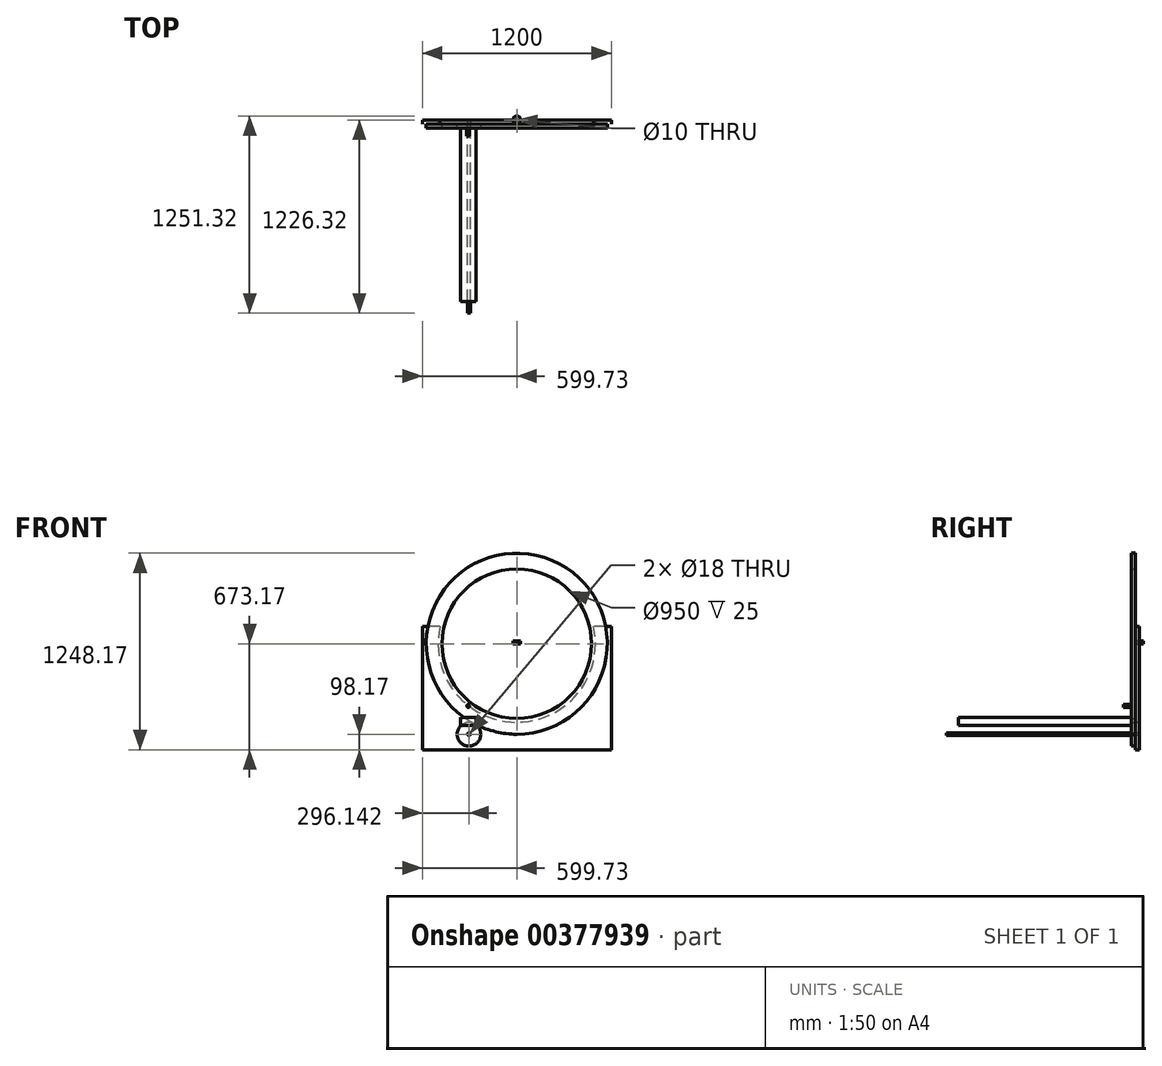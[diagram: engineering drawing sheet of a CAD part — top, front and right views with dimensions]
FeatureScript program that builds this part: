
annotation { "Feature Type Name" : "Feature", "Feature Type Description" : "" }
export const myFeature = defineFeature(function(context is Context, id is Id, definition is map)
    precondition{}
    {
        {
            var Q0;
            Q0=qCreatedBy(makeId("Front.planeOp"),FACE);
            var sketch = newSketch(context, id + "F0", { "sketchPlane" : qUnion([Q0])});
            skCircle(sketch, "E0", {"center": v(0, 0) * mm, "radius": 575 * mm});
            skCircle(sketch, "E1.0", {"center": v(0, 0) * mm, "radius": 475 * mm});
            skLineSegment(sketch, "E2", {"start": v(0, -575) * mm, "end": v(-1243.46, -575) * mm, "construction": true});
            skCircle(sketch, "E3", {"center": v(-303.59, -575) * mm, "radius": 75 * mm});
            skCircle(sketch, "E4", {"center": v(-303.59, -575) * mm, "radius": 9 * mm});
            skSolve(sketch);
        }
        {
            var Q0;
            Q0 = qSketchRegion(id + "F0", true);
            extrude(context, id + "F1", {"entities" : qUnion([Q0]), "depth" : 25 * mm});
        }
        {
            var Q0;
            Q0=makeQuery(id+"F0.imprint","IMPRINT",FACE,{"disambiguationData":[TD([[makeQuery(id+"F0.imprint","IMPRINT",EDGE,{"derivedFrom":sQuery(id+"F0.wireOp",EDGE,"E4")}),1.0]])]});
            extrude(context, id + "F2", {"entities" : qUnion([Q0]), "depth" : (48 * 25) * mm});
        }
        {
            var Q0;
            Q0=qCreatedBy(makeId("Top.planeOp"),FACE);
            var sketch = newSketch(context, id + "F3", { "sketchPlane" : qUnion([Q0])});
            skCircle(sketch, "E5", {"center": v(0, 26.32) * mm, "radius": 25 * mm});
            skCircle(sketch, "E6", {"center": v(0, 26.32) * mm, "radius": 5 * mm});
            skSolve(sketch);
        }
        {
            var Q0;
            Q0=makeQuery(id+"F3.imprint","IMPRINT",FACE,{"disambiguationData":[TD([[makeQuery(id+"F3.imprint","IMPRINT",EDGE,{"derivedFrom":sQuery(id+"F3.wireOp",EDGE,"E5")}),1.0]])]});
            extrude(context, id + "F4", {"entities" : qUnion([Q0]), "depth" : 18 * mm});
        }
        {
            var Q0;
            Q0=qCreatedBy(makeId("Front.planeOp"),FACE);
            var sketch = newSketch(context, id + "F5", { "sketchPlane" : qUnion([Q0])});
            skCircle(sketch, "E7", {"center": v(0, 0) * mm, "radius": 575 * mm});
            skCircle(sketch, "E8.0", {"center": v(0, 0) * mm, "radius": 475 * mm});
            skLineSegment(sketch, "E9", {"start": v(0, -575) * mm, "end": v(-1243.46, -575) * mm, "construction": true});
            skCircle(sketch, "E10", {"center": v(-303.59, -575) * mm, "radius": 75 * mm});
            skCircle(sketch, "E11", {"center": v(-303.59, -575) * mm, "radius": 9 * mm});
            skCircle(sketch, "E12", {"center": v(0, 0) * mm, "radius": 499.06 * mm});
            skPoint(sketch, "E13.firstSnap0", {"position": v(-621.73, -575) * mm});
            skLineSegment(sketch, "E13.bottom", {"start": v(-599.73, 526.83) * mm, "end": v(600.27, 526.83) * mm});
            skLineSegment(sketch, "E13.top", {"start": v(-599.73, -673.17) * mm, "end": v(600.27, -673.17) * mm});
            skLineSegment(sketch, "E13.left", {"start": v(-599.73, 526.83) * mm, "end": v(-599.73, -673.17) * mm});
            skLineSegment(sketch, "E13.right", {"start": v(600.27, 526.83) * mm, "end": v(600.27, -673.17) * mm});
            skLineSegment(sketch, "E14", {"start": v(707.26, 110.12) * mm, "end": v(-898.64, 110.12) * mm});
            skSolve(sketch);
        }
        {
            var Q0;
            Q0=makeQuery(id+"F5.imprint","IMPRINT",FACE,{"disambiguationData":[TD([[makeQuery(id+"F5.imprint","IMPRINT",EDGE,{"derivedFrom":sQuery(id+"F5.wireOp",EDGE,"E10")}),-1.0]])]});
            var Q1;
            {var subQ0=sQuery(id+"F5.wireOp",EDGE,"E14");var subQ1=sQuery(id+"F5.wireOp",EDGE,"E7");var subQ2=makeQuery(id+"F5.imprint","INTERSECT",VERTEX,{"disambiguationData":[OD(0.0)],"derivedFrom":[subQ1,subQ0]});Q1=makeQuery(id+"F5.imprint","IMPRINT",FACE,{"disambiguationData":[TD([[makeQuery(id+"F5.imprint","IMPRINT",EDGE,{"disambiguationData":[TD([[subQ2,1.0]])],"derivedFrom":subQ1}),1.0]])]});}
            var Q2;
            Q2=makeQuery(id+"F5.imprint","IMPRINT",FACE,{"disambiguationData":[TD([[makeQuery(id+"F5.imprint","IMPRINT",EDGE,{"derivedFrom":sQuery(id+"F5.wireOp",EDGE,"E10")}),1.0]])]});
            extrude(context, id + "F6", {"entities" : qUnion([Q0, Q1, Q2]), "oppositeDirection" : true, "depth" : 25 * mm});
        }
        {
            var Q0;
            Q0=makeQuery(id+"F1.opExtrude","CAP_FACE",FACE,{"disambiguationData":[OSD([sQuery(id+"F0.wireOp",EDGE,"E0"),sQuery(id+"F0.wireOp",EDGE,"E1.0")])],"isStart":false});
            var sketch = newSketch(context, id + "F7", { "sketchPlane" : qUnion([Q0])});
            skCircle(sketch, "E15", {"center": v(-308.72, -395.52) * mm, "radius": 9 * mm});
            skLineSegment(sketch, "E16.bottom", {"start": v(-258.72, -468.3) * mm, "end": v(-358.72, -468.3) * mm});
            skLineSegment(sketch, "E16.top", {"start": v(-258.72, -518.3) * mm, "end": v(-358.72, -518.3) * mm});
            skLineSegment(sketch, "E16.left", {"start": v(-258.72, -468.3) * mm, "end": v(-258.72, -518.3) * mm});
            skLineSegment(sketch, "E16.right", {"start": v(-358.72, -468.3) * mm, "end": v(-358.72, -518.3) * mm});
            skPoint(sketch, "E16.middle", {"position": v(-308.72, -493.3) * mm});
            skLineSegment(sketch, "E17", {"start": v(-358.72, -468.3) * mm, "end": v(-316.62, -391.2) * mm});
            skLineSegment(sketch, "E18", {"start": v(-258.72, -468.3) * mm, "end": v(-300.82, -391.2) * mm});
            skSolve(sketch);
        }
        {
            var Q0;
            {var subQ0=sQuery(id+"F7.wireOp",EDGE,"E15");var subQ1=makeQuery(id+"F7.imprint","INTERSECT",VERTEX,{"derivedFrom":[subQ0,sQuery(id+"F7.wireOp",EDGE,"E17")]});Q0=makeQuery(id+"F7.imprint","IMPRINT",FACE,{"disambiguationData":[TD([[makeQuery(id+"F7.imprint","IMPRINT",EDGE,{"disambiguationData":[TD([[subQ1,1.0]])],"derivedFrom":subQ0}),1.0]])]});}
            extrude(context, id + "F8", {"entities" : qUnion([Q0]), "depth" : 50 * mm});
        }
        {
            var Q0;
            {var subQ0=sQuery(id+"F7.wireOp",EDGE,"E16.left");var subQ3=makeQuery(id+"F1.opExtrude","CAP_EDGE",EDGE,{"disambiguationData":[OSD([sQuery(id+"F0.wireOp",EDGE,"E0")])],"isStart":false});var subQ5=makeQuery(id+"F7.imprint","INTERSECT",VERTEX,{"derivedFrom":[subQ3,subQ0]});Q0=makeQuery(id+"F7.imprint","IMPRINT",FACE,{"disambiguationData":[TD([[makeQuery(id+"F7.imprint","IMPRINT",EDGE,{"disambiguationData":[TD([[subQ5,1.0]])],"derivedFrom":subQ3}),1.0]])]});}
            var Q1;
            {var subQ2=sQuery(id+"F7.wireOp",EDGE,"E16.top");Q1=makeQuery(id+"F7.imprint","IMPRINT",FACE,{"disambiguationData":[TD([[makeQuery(id+"F7.imprint","IMPRINT",EDGE,{"derivedFrom":subQ2}),-1.0]])]});}
            extrude(context, id + "F9", {"entities" : qUnion([Q0, Q1]), "depth" : (44 * 25) * mm});
        }
    });
